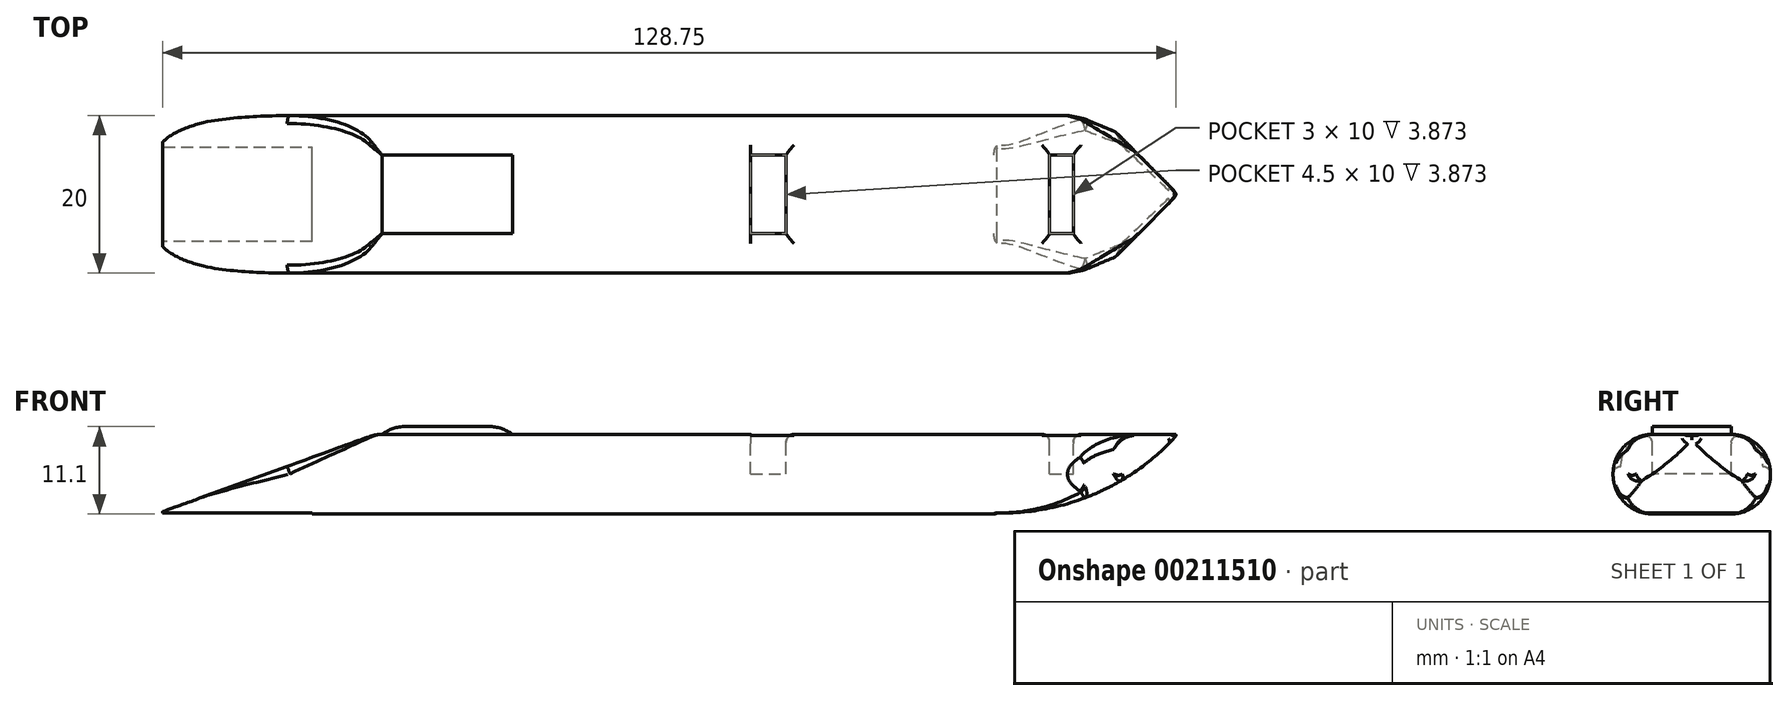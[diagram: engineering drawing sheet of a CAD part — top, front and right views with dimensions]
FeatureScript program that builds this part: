
annotation { "Feature Type Name" : "Feature", "Feature Type Description" : "" }
export const myFeature = defineFeature(function(context is Context, id is Id, definition is map)
    precondition{}
    {
        {
            var Q0;
            Q0=qCreatedBy(makeId("Top.planeOp"),FACE);
            var sketch = newSketch(context, id + "F0", { "sketchPlane" : qUnion([Q0])});
            skLineSegment(sketch, "E0.bottom", {"start": v(-64.41, 48.03) * mm, "end": v(65.59, 48.03) * mm});
            skLineSegment(sketch, "E0.top", {"start": v(-64.41, 28.03) * mm, "end": v(65.59, 28.03) * mm});
            skLineSegment(sketch, "E0.left", {"start": v(-64.41, 48.03) * mm, "end": v(-64.41, 28.03) * mm});
            skLineSegment(sketch, "E0.right", {"start": v(65.59, 48.03) * mm, "end": v(65.59, 28.03) * mm});
            skSolve(sketch);
        }
        {
            var Q0;
            Q0 = qSketchRegion(id + "F0", true);
            extrude(context, id + "F1", {"entities" : qUnion([Q0]), "depth" : 10 * mm});
        }
        {
            var Q0;
            Q0=makeQuery(id+"F1.opExtrude","CAP_EDGE",EDGE,{"disambiguationData":[OSD([sQuery(id+"F0.wireOp",EDGE,"E0.left")])],"isStart":false});
            chamfer(context, id + "F2", {"entities" : qUnion([Q0]), "chamferType" : ChamferType.OFFSET_ANGLE, "width" : 28 * mm, "oppositeDirection" : false, "angle" : 20 * degree, "tangentPropagation" : true});
        }
        {
            var Q0;
            Q0=makeQuery(id+"F1.opExtrude","SWEPT_EDGE",EDGE,{"disambiguationData":[OSD([sQuery(id+"F0.wireOp",EDGE,"E0.bottom"),sQuery(id+"F0.wireOp",EDGE,"E0.right")])]});
            var Q1;
            Q1=makeQuery(id+"F1.opExtrude","CAP_EDGE",EDGE,{"disambiguationData":[OSD([sQuery(id+"F0.wireOp",EDGE,"E0.right")])],"isStart":true});
            var Q2;
            Q2=makeQuery(id+"F1.opExtrude","SWEPT_EDGE",EDGE,{"disambiguationData":[OSD([sQuery(id+"F0.wireOp",EDGE,"E0.top"),sQuery(id+"F0.wireOp",EDGE,"E0.right")])]});
            chamfer(context, id + "F3", {"entities" : qUnion([Q0, Q1, Q2]), "chamferType" : ChamferType.OFFSET_ANGLE, "width" : 10 * mm, "oppositeDirection" : false, "angle" : 45 * degree, "tangentPropagation" : true});
        }
        {
            var Q0;
            {var subQ0=sQuery(id+"F0.wireOp",EDGE,"E0.right");Q0=makeQuery(id+"F3.opChamfer","BLEND_EDGE",EDGE,{"blendedFrom":[makeQuery(id+"F1.opExtrude","CAP_EDGE",EDGE,{"disambiguationData":[OSD([subQ0])],"isStart":true}),makeQuery(id+"F1.opExtrude","CAP_FACE",FACE,{"disambiguationData":[OSD([sQuery(id+"F0.wireOp",EDGE,"E0.bottom"),sQuery(id+"F0.wireOp",EDGE,"E0.top"),sQuery(id+"F0.wireOp",EDGE,"E0.left"),subQ0])],"isStart":true})],"blendedInto":[makeQuery(id+"F1.opExtrude","CAP_FACE",FACE,{"disambiguationData":[OSD([sQuery(id+"F0.wireOp",EDGE,"E0.bottom"),sQuery(id+"F0.wireOp",EDGE,"E0.top"),sQuery(id+"F0.wireOp",EDGE,"E0.left"),subQ0])],"isStart":true})]});}
            fillet(context, id + "F4", {"entities" : qUnion([Q0]), "radius" : 30 * mm, "tangentPropagation" : true, "allowEdgeOverflow" : false});
        }
        {
            var Q0;
            {var subQ0=sQuery(id+"F0.wireOp",EDGE,"E0.top");Q0=makeQuery(id+"F3.opChamfer","BLEND_EDGE",EDGE,{"blendedFrom":[makeQuery(id+"F1.opExtrude","SWEPT_EDGE",EDGE,{"disambiguationData":[OSD([subQ0,sQuery(id+"F0.wireOp",EDGE,"E0.right")])]}),makeQuery(id+"F1.opExtrude","SWEPT_FACE",FACE,{"disambiguationData":[OSD([subQ0])]})],"blendedInto":[makeQuery(id+"F1.opExtrude","SWEPT_FACE",FACE,{"disambiguationData":[OSD([subQ0])]})]});}
            var Q1;
            {var subQ0=sQuery(id+"F0.wireOp",EDGE,"E0.bottom");Q1=makeQuery(id+"F3.opChamfer","BLEND_EDGE",EDGE,{"blendedFrom":[makeQuery(id+"F1.opExtrude","SWEPT_EDGE",EDGE,{"disambiguationData":[OSD([subQ0,sQuery(id+"F0.wireOp",EDGE,"E0.right")])]}),makeQuery(id+"F1.opExtrude","SWEPT_FACE",FACE,{"disambiguationData":[OSD([subQ0])]})],"blendedInto":[makeQuery(id+"F1.opExtrude","SWEPT_FACE",FACE,{"disambiguationData":[OSD([subQ0])]})]});}
            chamfer(context, id + "F5", {"entities" : qUnion([Q0, Q1]), "width" : 7 * mm, "tangentPropagation" : true});
        }
        {
            var Q0;
            {var subQ0=sQuery(id+"F0.wireOp",EDGE,"E0.top");var subQ1=makeQuery(id+"F1.opExtrude","SWEPT_FACE",FACE,{"disambiguationData":[OSD([subQ0])]});Q0=makeQuery(id+"F5.opChamfer","BLEND_EDGE",EDGE,{"blendedFrom":[makeQuery(id+"F3.opChamfer","BLEND_EDGE",EDGE,{"blendedFrom":[makeQuery(id+"F1.opExtrude","SWEPT_EDGE",EDGE,{"disambiguationData":[OSD([subQ0,sQuery(id+"F0.wireOp",EDGE,"E0.right")])]}),subQ1],"blendedInto":[subQ1]}),subQ1],"blendedInto":[subQ1]});}
            var Q1;
            {var subQ0=sQuery(id+"F0.wireOp",EDGE,"E0.bottom");var subQ1=makeQuery(id+"F1.opExtrude","SWEPT_FACE",FACE,{"disambiguationData":[OSD([subQ0])]});Q1=makeQuery(id+"F5.opChamfer","BLEND_EDGE",EDGE,{"blendedFrom":[makeQuery(id+"F3.opChamfer","BLEND_EDGE",EDGE,{"blendedFrom":[makeQuery(id+"F1.opExtrude","SWEPT_EDGE",EDGE,{"disambiguationData":[OSD([subQ0,sQuery(id+"F0.wireOp",EDGE,"E0.right")])]}),subQ1],"blendedInto":[subQ1]}),subQ1],"blendedInto":[subQ1]});}
            chamfer(context, id + "F6", {"entities" : qUnion([Q0, Q1]), "width" : 5 * mm, "tangentPropagation" : true});
        }
        {
            var Q0;
            Q0=makeQuery(id+"F2.opChamfer","BLEND_EDGE",EDGE,{"blendedFrom":[makeQuery(id+"F1.opExtrude","CAP_EDGE",EDGE,{"disambiguationData":[OSD([sQuery(id+"F0.wireOp",EDGE,"E0.left")])],"isStart":false}),makeQuery(id+"F1.opExtrude","SWEPT_FACE",FACE,{"disambiguationData":[OSD([sQuery(id+"F0.wireOp",EDGE,"E0.top")])]})],"blendedInto":[makeQuery(id+"F1.opExtrude","SWEPT_FACE",FACE,{"disambiguationData":[OSD([sQuery(id+"F0.wireOp",EDGE,"E0.top")])]})]});
            var Q1;
            Q1=makeQuery(id+"F2.opChamfer","BLEND_EDGE",EDGE,{"blendedFrom":[makeQuery(id+"F1.opExtrude","CAP_EDGE",EDGE,{"disambiguationData":[OSD([sQuery(id+"F0.wireOp",EDGE,"E0.left")])],"isStart":false}),makeQuery(id+"F1.opExtrude","SWEPT_FACE",FACE,{"disambiguationData":[OSD([sQuery(id+"F0.wireOp",EDGE,"E0.bottom")])]})],"blendedInto":[makeQuery(id+"F1.opExtrude","SWEPT_FACE",FACE,{"disambiguationData":[OSD([sQuery(id+"F0.wireOp",EDGE,"E0.bottom")])]})]});
            fillet(context, id + "F7", {"entities" : qUnion([Q0, Q1]), "radius" : 1 * mm, "tangentPropagation" : true, "allowEdgeOverflow" : false});
        }
        {
            var Q0;
            {var subQ0=sQuery(id+"F0.wireOp",EDGE,"E0.left");Q0=makeQuery(id+"F2.opChamfer","BLEND_EDGE",EDGE,{"blendedFrom":[makeQuery(id+"F1.opExtrude","CAP_EDGE",EDGE,{"disambiguationData":[OSD([subQ0])],"isStart":false}),makeQuery(id+"F1.opExtrude","CAP_FACE",FACE,{"disambiguationData":[OSD([sQuery(id+"F0.wireOp",EDGE,"E0.bottom"),sQuery(id+"F0.wireOp",EDGE,"E0.top"),subQ0,sQuery(id+"F0.wireOp",EDGE,"E0.right")])],"isStart":false})],"blendedInto":[makeQuery(id+"F1.opExtrude","CAP_FACE",FACE,{"disambiguationData":[OSD([sQuery(id+"F0.wireOp",EDGE,"E0.bottom"),sQuery(id+"F0.wireOp",EDGE,"E0.top"),subQ0,sQuery(id+"F0.wireOp",EDGE,"E0.right")])],"isStart":false})]});}
            fillet(context, id + "F8", {"entities" : qUnion([Q0]), "radius" : 5 * mm, "tangentPropagation" : true, "allowEdgeOverflow" : false});
        }
        {
            var Q0;
            Q0=makeQuery(id+"F1.opExtrude","CAP_FACE",FACE,{"disambiguationData":[OSD([sQuery(id+"F0.wireOp",EDGE,"E0.bottom"),sQuery(id+"F0.wireOp",EDGE,"E0.top"),sQuery(id+"F0.wireOp",EDGE,"E0.left"),sQuery(id+"F0.wireOp",EDGE,"E0.right")])],"isStart":false});
            var sketch = newSketch(context, id + "F9", { "sketchPlane" : qUnion([Q0])});
            skLineSegment(sketch, "E1.bottom", {"start": v(52.29, 43.03) * mm, "end": v(49.29, 43.03) * mm});
            skLineSegment(sketch, "E1.top", {"start": v(52.29, 33.03) * mm, "end": v(49.29, 33.03) * mm});
            skLineSegment(sketch, "E1.left", {"start": v(52.29, 43.03) * mm, "end": v(52.29, 33.03) * mm});
            skLineSegment(sketch, "E1.right", {"start": v(49.29, 43.03) * mm, "end": v(49.29, 33.03) * mm});
            skLineSegment(sketch, "E2.bottom", {"start": v(-31.53, 43.03) * mm, "end": v(-23.03, 43.03) * mm});
            skLineSegment(sketch, "E2.top", {"start": v(-31.53, 33.03) * mm, "end": v(-23.03, 33.03) * mm});
            skLineSegment(sketch, "E2.left", {"start": v(-31.53, 43.03) * mm, "end": v(-31.53, 33.03) * mm});
            skLineSegment(sketch, "E2.right", {"start": v(-23.03, 43.03) * mm, "end": v(-23.03, 33.03) * mm});
            skLineSegment(sketch, "E3.bottom", {"start": v(11.3, 43.03) * mm, "end": v(15.8, 43.03) * mm});
            skLineSegment(sketch, "E3.top", {"start": v(11.3, 33.03) * mm, "end": v(15.8, 33.03) * mm});
            skLineSegment(sketch, "E3.left", {"start": v(11.3, 43.03) * mm, "end": v(11.3, 33.03) * mm});
            skLineSegment(sketch, "E3.right", {"start": v(15.8, 43.03) * mm, "end": v(15.8, 33.03) * mm});
            skSolve(sketch);
        }
        {
            var Q0;
            Q0=makeQuery(id+"F9.imprint","IMPRINT",FACE,{"disambiguationData":[TD([[makeQuery(id+"F9.imprint","IMPRINT",EDGE,{"derivedFrom":sQuery(id+"F9.wireOp",EDGE,"E3.bottom")}),1.0]])]});
            var Q1;
            Q1=makeQuery(id+"F9.imprint","IMPRINT",FACE,{"disambiguationData":[TD([[makeQuery(id+"F9.imprint","IMPRINT",EDGE,{"derivedFrom":sQuery(id+"F9.wireOp",EDGE,"E1.bottom")}),1.0]])]});
            extrude(context, id + "F10", {"entities" : qUnion([Q0, Q1]), "operationType" : NewBodyOperationType.REMOVE, "oppositeDirection" : true, "depth" : 5 * mm});
        }
        {
            var Q0;
            {var subQ0=sQuery(id+"F0.wireOp",EDGE,"E0.right");var subQ1=sQuery(id+"F0.wireOp",EDGE,"E0.top");Q0=makeQuery(id+"F4.opFillet","BLEND_EDGE",EDGE,{"blendedFrom":[makeQuery(id+"F3.opChamfer","BLEND_EDGE",EDGE,{"blendedFrom":[makeQuery(id+"F1.opExtrude","CAP_EDGE",EDGE,{"disambiguationData":[OSD([subQ0])],"isStart":true}),makeQuery(id+"F1.opExtrude","CAP_FACE",FACE,{"disambiguationData":[OSD([sQuery(id+"F0.wireOp",EDGE,"E0.bottom"),subQ1,sQuery(id+"F0.wireOp",EDGE,"E0.left"),subQ0])],"isStart":true})],"blendedInto":[makeQuery(id+"F1.opExtrude","CAP_FACE",FACE,{"disambiguationData":[OSD([sQuery(id+"F0.wireOp",EDGE,"E0.bottom"),subQ1,sQuery(id+"F0.wireOp",EDGE,"E0.left"),subQ0])],"isStart":true})]}),makeQuery(id+"F3.opChamfer","BLEND_FACE",FACE,{"disambiguationData":[OSD([subQ1,subQ0])]})],"blendedInto":[makeQuery(id+"F3.opChamfer","BLEND_FACE",FACE,{"disambiguationData":[OSD([subQ1,subQ0])]})]});}
            var Q1;
            {var subQ0=sQuery(id+"F0.wireOp",EDGE,"E0.right");var subQ1=sQuery(id+"F0.wireOp",EDGE,"E0.bottom");Q1=makeQuery(id+"F4.opFillet","BLEND_EDGE",EDGE,{"blendedFrom":[makeQuery(id+"F3.opChamfer","BLEND_EDGE",EDGE,{"blendedFrom":[makeQuery(id+"F1.opExtrude","CAP_EDGE",EDGE,{"disambiguationData":[OSD([subQ0])],"isStart":true}),makeQuery(id+"F1.opExtrude","CAP_FACE",FACE,{"disambiguationData":[OSD([subQ1,sQuery(id+"F0.wireOp",EDGE,"E0.top"),sQuery(id+"F0.wireOp",EDGE,"E0.left"),subQ0])],"isStart":true})],"blendedInto":[makeQuery(id+"F1.opExtrude","CAP_FACE",FACE,{"disambiguationData":[OSD([subQ1,sQuery(id+"F0.wireOp",EDGE,"E0.top"),sQuery(id+"F0.wireOp",EDGE,"E0.left"),subQ0])],"isStart":true})]}),makeQuery(id+"F3.opChamfer","BLEND_FACE",FACE,{"disambiguationData":[OSD([subQ1,subQ0])]})],"blendedInto":[makeQuery(id+"F3.opChamfer","BLEND_FACE",FACE,{"disambiguationData":[OSD([subQ1,subQ0])]})]});}
            fillet(context, id + "F11", {"entities" : qUnion([Q0, Q1]), "radius" : 1 * mm, "tangentPropagation" : true, "allowEdgeOverflow" : false});
        }
        {
            var Q0;
            {var subQ0=sQuery(id+"F0.wireOp",EDGE,"E0.bottom");var subQ1=sQuery(id+"F0.wireOp",EDGE,"E0.right");var subQ2=sQuery(id+"F0.wireOp",EDGE,"E0.left");var subQ3=sQuery(id+"F0.wireOp",EDGE,"E0.top");var subQ4=makeQuery(id+"F1.opExtrude","CAP_FACE",FACE,{"disambiguationData":[OSD([subQ0,subQ3,subQ2,subQ1])],"isStart":false});var subQ5=subQ4;Q0=makeQuery(id+"F10.boolean.opBoolean","SPLIT",FACE,{"disambiguationData":[TD([makeQuery(id+"F10.opExtrude","SWEPT_FACE",FACE,{"disambiguationData":[OSD([sQuery(id+"F9.wireOp",EDGE,"E3.left")])]})])],"derivedFrom":subQ5});}
            var sketch = newSketch(context, id + "F12", { "sketchPlane" : qUnion([Q0])});
            skLineSegment(sketch, "E4", {"start": v(-18.95, 33.03) * mm, "end": v(-18.95, 43.03) * mm});
            skSolve(sketch);
        }
        {
            var Q0;
            {var subQ0=sQuery(id+"F12.wireOp",EDGE,"E4");Q0=makeQuery(id+"F12.imprint","IMPRINT",FACE,{"disambiguationData":[TD([[makeQuery(id+"F12.imprint","IMPRINT",EDGE,{"derivedFrom":subQ0}),1.0]])]});}
            extrude(context, id + "F13", {"entities" : qUnion([Q0]), "operationType" : NewBodyOperationType.ADD, "depth" : 1 * mm});
        }
        {
            var Q0;
            Q0=makeQuery(id+"F13.opExtrude","CAP_EDGE",EDGE,{"disambiguationData":[OSD([sQuery(id+"F12.wireOp",EDGE,"E4")])],"isStart":false});
            fillet(context, id + "F14", {"entities" : qUnion([Q0]), "radius" : 5 * mm, "tangentPropagation" : true, "allowEdgeOverflow" : false});
        }
        {
            var Q0;
            {var subQ0=sQuery(id+"F0.wireOp",EDGE,"E0.right");var subQ1=sQuery(id+"F0.wireOp",EDGE,"E0.left");var subQ2=sQuery(id+"F0.wireOp",EDGE,"E0.top");var subQ3=sQuery(id+"F0.wireOp",EDGE,"E0.bottom");var subQ4=makeQuery(id+"F1.opExtrude","CAP_FACE",FACE,{"disambiguationData":[OSD([subQ3,subQ2,subQ1,subQ0])],"isStart":false});Q0=makeQuery(id+"F13.opExtrude","CAP_EDGE",EDGE,{"disambiguationData":[OSD([subQ3,subQ2,subQ1,subQ0]),TDD([makeQuery(id+"F12.imprint","IMPRINT",EDGE,{"derivedFrom":makeQuery(id+"F8.opFillet","BLEND_EDGE",EDGE,{"blendedFrom":[makeQuery(id+"F2.opChamfer","BLEND_EDGE",EDGE,{"blendedFrom":[makeQuery(id+"F1.opExtrude","CAP_EDGE",EDGE,{"disambiguationData":[OSD([subQ1])],"isStart":false}),subQ4],"blendedInto":[subQ4]}),subQ4],"blendedInto":[subQ4]})})])],"isStart":false});}
            fillet(context, id + "F15", {"entities" : qUnion([Q0]), "radius" : 5 * mm, "tangentPropagation" : true, "allowEdgeOverflow" : false});
        }
        {
            var Q0;
            Q0=makeQuery(id+"F1.opExtrude","CAP_FACE",FACE,{"disambiguationData":[OSD([sQuery(id+"F0.wireOp",EDGE,"E0.bottom"),sQuery(id+"F0.wireOp",EDGE,"E0.top"),sQuery(id+"F0.wireOp",EDGE,"E0.left"),sQuery(id+"F0.wireOp",EDGE,"E0.right")])],"isStart":true});
            var sketch = newSketch(context, id + "F16", { "sketchPlane" : qUnion([Q0])});
            skLineSegment(sketch, "E5.bottom", {"start": v(-44.4, -28.03) * mm, "end": v(42.6, -28.03) * mm});
            skLineSegment(sketch, "E5.top", {"start": v(-44.4, -48.03) * mm, "end": v(42.6, -48.03) * mm});
            skLineSegment(sketch, "E5.left", {"start": v(-44.4, -28.03) * mm, "end": v(-44.4, -48.03) * mm});
            skLineSegment(sketch, "E5.right", {"start": v(42.6, -28.03) * mm, "end": v(42.6, -48.03) * mm});
            skSolve(sketch);
        }
        {
            var Q0;
            Q0 = qSketchRegion(id + "F16", true);
            extrude(context, id + "F17", {"entities" : qUnion([Q0]), "operationType" : NewBodyOperationType.ADD, "depth" : 0.1 * mm});
        }
        {
            var Q0;
            Q0=makeQuery(id+"F17.opExtrude","CAP_EDGE",EDGE,{"disambiguationData":[OSD([sQuery(id+"F16.wireOp",EDGE,"E5.bottom")])],"isStart":false});
            var Q1;
            Q1=makeQuery(id+"F17.opExtrude","CAP_EDGE",EDGE,{"disambiguationData":[OSD([sQuery(id+"F16.wireOp",EDGE,"E5.top")])],"isStart":false});
            fillet(context, id + "F18", {"entities" : qUnion([Q0, Q1]), "radius" : 5 * mm, "tangentPropagation" : true, "allowEdgeOverflow" : false});
        }
        {
            var Q0;
            {var subQ0=sQuery(id+"F0.wireOp",EDGE,"E0.right");var subQ1=sQuery(id+"F0.wireOp",EDGE,"E0.top");Q0=makeQuery(id+"F3.opChamfer","BLEND_EDGE",EDGE,{"blendedFrom":[makeQuery(id+"F1.opExtrude","SWEPT_EDGE",EDGE,{"disambiguationData":[OSD([subQ1,subQ0])]}),makeQuery(id+"F1.opExtrude","CAP_FACE",FACE,{"disambiguationData":[OSD([sQuery(id+"F0.wireOp",EDGE,"E0.bottom"),subQ1,sQuery(id+"F0.wireOp",EDGE,"E0.left"),subQ0])],"isStart":false})],"blendedInto":[makeQuery(id+"F1.opExtrude","CAP_FACE",FACE,{"disambiguationData":[OSD([sQuery(id+"F0.wireOp",EDGE,"E0.bottom"),subQ1,sQuery(id+"F0.wireOp",EDGE,"E0.left"),subQ0])],"isStart":false})]});}
            var Q1;
            {var subQ0=sQuery(id+"F0.wireOp",EDGE,"E0.right");var subQ1=sQuery(id+"F0.wireOp",EDGE,"E0.bottom");Q1=makeQuery(id+"F3.opChamfer","BLEND_EDGE",EDGE,{"blendedFrom":[makeQuery(id+"F1.opExtrude","SWEPT_EDGE",EDGE,{"disambiguationData":[OSD([subQ1,subQ0])]}),makeQuery(id+"F1.opExtrude","CAP_FACE",FACE,{"disambiguationData":[OSD([subQ1,sQuery(id+"F0.wireOp",EDGE,"E0.top"),sQuery(id+"F0.wireOp",EDGE,"E0.left"),subQ0])],"isStart":false})],"blendedInto":[makeQuery(id+"F1.opExtrude","CAP_FACE",FACE,{"disambiguationData":[OSD([subQ1,sQuery(id+"F0.wireOp",EDGE,"E0.top"),sQuery(id+"F0.wireOp",EDGE,"E0.left"),subQ0])],"isStart":false})]});}
            var Q2;
            {var subQ0=sQuery(id+"F0.wireOp",EDGE,"E0.right");var subQ1=sQuery(id+"F0.wireOp",EDGE,"E0.top");var subQ2=makeQuery(id+"F1.opExtrude","SWEPT_FACE",FACE,{"disambiguationData":[OSD([subQ1])]});Q2=makeQuery(id+"F6.opChamfer","BLEND_EDGE",EDGE,{"blendedFrom":[makeQuery(id+"F5.opChamfer","BLEND_EDGE",EDGE,{"blendedFrom":[makeQuery(id+"F3.opChamfer","BLEND_EDGE",EDGE,{"blendedFrom":[makeQuery(id+"F1.opExtrude","SWEPT_EDGE",EDGE,{"disambiguationData":[OSD([subQ1,subQ0])]}),subQ2],"blendedInto":[subQ2]}),subQ2],"blendedInto":[subQ2]}),makeQuery(id+"F5.opChamfer","BLEND_FACE",FACE,{"disambiguationData":[OSD([subQ1,subQ0])]})],"blendedInto":[makeQuery(id+"F5.opChamfer","BLEND_FACE",FACE,{"disambiguationData":[OSD([subQ1,subQ0])]})]});}
            var Q3;
            {var subQ0=sQuery(id+"F0.wireOp",EDGE,"E0.right");var subQ1=sQuery(id+"F0.wireOp",EDGE,"E0.bottom");var subQ2=makeQuery(id+"F1.opExtrude","SWEPT_FACE",FACE,{"disambiguationData":[OSD([subQ1])]});Q3=makeQuery(id+"F6.opChamfer","BLEND_EDGE",EDGE,{"blendedFrom":[makeQuery(id+"F5.opChamfer","BLEND_EDGE",EDGE,{"blendedFrom":[makeQuery(id+"F3.opChamfer","BLEND_EDGE",EDGE,{"blendedFrom":[makeQuery(id+"F1.opExtrude","SWEPT_EDGE",EDGE,{"disambiguationData":[OSD([subQ1,subQ0])]}),subQ2],"blendedInto":[subQ2]}),subQ2],"blendedInto":[subQ2]}),makeQuery(id+"F5.opChamfer","BLEND_FACE",FACE,{"disambiguationData":[OSD([subQ1,subQ0])]})],"blendedInto":[makeQuery(id+"F5.opChamfer","BLEND_FACE",FACE,{"disambiguationData":[OSD([subQ1,subQ0])]})]});}
            fillet(context, id + "F19", {"entities" : qUnion([Q0, Q1, Q2, Q3]), "radius" : 0.1 * mm, "tangentPropagation" : true, "allowEdgeOverflow" : false});
        }
        {
            var Q0;
            Q0=makeQuery(id+"F10.boolean.opBoolean","COPY",EDGE,{"derivedFrom":makeQuery(id+"F10.opExtrude","CAP_EDGE",EDGE,{"disambiguationData":[OSD([sQuery(id+"F9.wireOp",EDGE,"E1.right")])],"isStart":true})});
            var Q1;
            {var subQ0=sQuery(id+"F0.wireOp",EDGE,"E0.bottom");Q1=makeQuery(id+"F10.boolean.opBoolean","MERGE",EDGE,{"derivedFrom":[makeQuery(id+"F8.opFillet","BLEND_EDGE",EDGE,{"blendedFrom":[makeQuery(id+"F1.opExtrude","CAP_EDGE",EDGE,{"disambiguationData":[OSD([subQ0])],"isStart":false}),makeQuery(id+"F1.opExtrude","CAP_FACE",FACE,{"disambiguationData":[OSD([subQ0,sQuery(id+"F0.wireOp",EDGE,"E0.top"),sQuery(id+"F0.wireOp",EDGE,"E0.left"),sQuery(id+"F0.wireOp",EDGE,"E0.right")])],"isStart":false})],"blendedInto":[makeQuery(id+"F1.opExtrude","CAP_FACE",FACE,{"disambiguationData":[OSD([subQ0,sQuery(id+"F0.wireOp",EDGE,"E0.top"),sQuery(id+"F0.wireOp",EDGE,"E0.left"),sQuery(id+"F0.wireOp",EDGE,"E0.right")])],"isStart":false})]}),makeQuery(id+"F10.opExtrude","CAP_EDGE",EDGE,{"disambiguationData":[OSD([sQuery(id+"F9.wireOp",EDGE,"E1.bottom")])],"isStart":true})]});}
            var Q2;
            Q2=makeQuery(id+"F10.boolean.opBoolean","COPY",EDGE,{"derivedFrom":makeQuery(id+"F10.opExtrude","CAP_EDGE",EDGE,{"disambiguationData":[OSD([sQuery(id+"F9.wireOp",EDGE,"E1.left")])],"isStart":true})});
            var Q3;
            {var subQ0=sQuery(id+"F0.wireOp",EDGE,"E0.top");Q3=makeQuery(id+"F10.boolean.opBoolean","MERGE",EDGE,{"derivedFrom":[makeQuery(id+"F8.opFillet","BLEND_EDGE",EDGE,{"blendedFrom":[makeQuery(id+"F1.opExtrude","CAP_EDGE",EDGE,{"disambiguationData":[OSD([subQ0])],"isStart":false}),makeQuery(id+"F1.opExtrude","CAP_FACE",FACE,{"disambiguationData":[OSD([sQuery(id+"F0.wireOp",EDGE,"E0.bottom"),subQ0,sQuery(id+"F0.wireOp",EDGE,"E0.left"),sQuery(id+"F0.wireOp",EDGE,"E0.right")])],"isStart":false})],"blendedInto":[makeQuery(id+"F1.opExtrude","CAP_FACE",FACE,{"disambiguationData":[OSD([sQuery(id+"F0.wireOp",EDGE,"E0.bottom"),subQ0,sQuery(id+"F0.wireOp",EDGE,"E0.left"),sQuery(id+"F0.wireOp",EDGE,"E0.right")])],"isStart":false})]}),makeQuery(id+"F10.opExtrude","CAP_EDGE",EDGE,{"disambiguationData":[OSD([sQuery(id+"F9.wireOp",EDGE,"E1.top")])],"isStart":true})]});}
            fillet(context, id + "F20", {"entities" : qUnion([Q0, Q1, Q2, Q3]), "radius" : 1 * mm, "tangentPropagation" : true, "allowEdgeOverflow" : false});
        }
        {
            var Q0;
            Q0=makeQuery(id+"F10.boolean.opBoolean","COPY",EDGE,{"derivedFrom":makeQuery(id+"F10.opExtrude","CAP_EDGE",EDGE,{"disambiguationData":[OSD([sQuery(id+"F9.wireOp",EDGE,"E3.left")])],"isStart":true})});
            var Q1;
            Q1=makeQuery(id+"F10.boolean.opBoolean","COPY",EDGE,{"derivedFrom":makeQuery(id+"F10.opExtrude","CAP_EDGE",EDGE,{"disambiguationData":[OSD([sQuery(id+"F9.wireOp",EDGE,"E3.right")])],"isStart":true})});
            var Q2;
            {var subQ0=sQuery(id+"F0.wireOp",EDGE,"E0.top");Q2=makeQuery(id+"F10.boolean.opBoolean","MERGE",EDGE,{"derivedFrom":[makeQuery(id+"F8.opFillet","BLEND_EDGE",EDGE,{"blendedFrom":[makeQuery(id+"F1.opExtrude","CAP_EDGE",EDGE,{"disambiguationData":[OSD([subQ0])],"isStart":false}),makeQuery(id+"F1.opExtrude","CAP_FACE",FACE,{"disambiguationData":[OSD([sQuery(id+"F0.wireOp",EDGE,"E0.bottom"),subQ0,sQuery(id+"F0.wireOp",EDGE,"E0.left"),sQuery(id+"F0.wireOp",EDGE,"E0.right")])],"isStart":false})],"blendedInto":[makeQuery(id+"F1.opExtrude","CAP_FACE",FACE,{"disambiguationData":[OSD([sQuery(id+"F0.wireOp",EDGE,"E0.bottom"),subQ0,sQuery(id+"F0.wireOp",EDGE,"E0.left"),sQuery(id+"F0.wireOp",EDGE,"E0.right")])],"isStart":false})]}),makeQuery(id+"F10.opExtrude","CAP_EDGE",EDGE,{"disambiguationData":[OSD([sQuery(id+"F9.wireOp",EDGE,"E3.top")])],"isStart":true})]});}
            var Q3;
            {var subQ0=sQuery(id+"F0.wireOp",EDGE,"E0.bottom");Q3=makeQuery(id+"F10.boolean.opBoolean","MERGE",EDGE,{"derivedFrom":[makeQuery(id+"F8.opFillet","BLEND_EDGE",EDGE,{"blendedFrom":[makeQuery(id+"F1.opExtrude","CAP_EDGE",EDGE,{"disambiguationData":[OSD([subQ0])],"isStart":false}),makeQuery(id+"F1.opExtrude","CAP_FACE",FACE,{"disambiguationData":[OSD([subQ0,sQuery(id+"F0.wireOp",EDGE,"E0.top"),sQuery(id+"F0.wireOp",EDGE,"E0.left"),sQuery(id+"F0.wireOp",EDGE,"E0.right")])],"isStart":false})],"blendedInto":[makeQuery(id+"F1.opExtrude","CAP_FACE",FACE,{"disambiguationData":[OSD([subQ0,sQuery(id+"F0.wireOp",EDGE,"E0.top"),sQuery(id+"F0.wireOp",EDGE,"E0.left"),sQuery(id+"F0.wireOp",EDGE,"E0.right")])],"isStart":false})]}),makeQuery(id+"F10.opExtrude","CAP_EDGE",EDGE,{"disambiguationData":[OSD([sQuery(id+"F9.wireOp",EDGE,"E3.bottom")])],"isStart":true})]});}
            fillet(context, id + "F21", {"entities" : qUnion([Q0, Q1, Q2, Q3]), "radius" : 1 * mm, "tangentPropagation" : true, "allowEdgeOverflow" : false});
        }
        {
            var Q0;
            {var subQ0=sQuery(id+"F0.wireOp",EDGE,"E0.right");var subQ1=sQuery(id+"F0.wireOp",EDGE,"E0.top");Q0=makeQuery(id+"F5.opChamfer","BLEND_EDGE",EDGE,{"blendedFrom":[makeQuery(id+"F3.opChamfer","BLEND_EDGE",EDGE,{"blendedFrom":[makeQuery(id+"F1.opExtrude","SWEPT_EDGE",EDGE,{"disambiguationData":[OSD([subQ1,subQ0])]}),makeQuery(id+"F1.opExtrude","SWEPT_FACE",FACE,{"disambiguationData":[OSD([subQ1])]})],"blendedInto":[makeQuery(id+"F1.opExtrude","SWEPT_FACE",FACE,{"disambiguationData":[OSD([subQ1])]})]}),makeQuery(id+"F3.opChamfer","BLEND_FACE",FACE,{"disambiguationData":[OSD([subQ1,subQ0])]})],"blendedInto":[makeQuery(id+"F3.opChamfer","BLEND_FACE",FACE,{"disambiguationData":[OSD([subQ1,subQ0])]})]});}
            var Q1;
            {var subQ0=sQuery(id+"F0.wireOp",EDGE,"E0.right");var subQ1=sQuery(id+"F0.wireOp",EDGE,"E0.top");Q1=makeQuery(id+"F5.opChamfer","BLEND_EDGE",EDGE,{"blendedFrom":[makeQuery(id+"F3.opChamfer","BLEND_EDGE",EDGE,{"blendedFrom":[makeQuery(id+"F1.opExtrude","SWEPT_EDGE",EDGE,{"disambiguationData":[OSD([subQ1,subQ0])]}),makeQuery(id+"F1.opExtrude","SWEPT_FACE",FACE,{"disambiguationData":[OSD([subQ1])]})],"blendedInto":[makeQuery(id+"F1.opExtrude","SWEPT_FACE",FACE,{"disambiguationData":[OSD([subQ1])]})]}),makeQuery(id+"F4.opFillet","BLEND_FACE",FACE,{"disambiguationData":[OSD([sQuery(id+"F0.wireOp",EDGE,"E0.bottom"),subQ1,sQuery(id+"F0.wireOp",EDGE,"E0.left"),subQ0])]})],"blendedInto":[makeQuery(id+"F4.opFillet","BLEND_FACE",FACE,{"disambiguationData":[OSD([sQuery(id+"F0.wireOp",EDGE,"E0.bottom"),subQ1,sQuery(id+"F0.wireOp",EDGE,"E0.left"),subQ0])]})]});}
            var Q2;
            Q2=makeQuery(id+"F18.opFillet","BLEND_EDGE",EDGE,{"blendedFrom":[makeQuery(id+"F17.opExtrude","CAP_EDGE",EDGE,{"disambiguationData":[OSD([sQuery(id+"F16.wireOp",EDGE,"E5.bottom")])],"isStart":false}),makeQuery(id+"F4.opFillet","BLEND_FACE",FACE,{"disambiguationData":[OSD([sQuery(id+"F0.wireOp",EDGE,"E0.bottom"),sQuery(id+"F0.wireOp",EDGE,"E0.top"),sQuery(id+"F0.wireOp",EDGE,"E0.left"),sQuery(id+"F0.wireOp",EDGE,"E0.right")])]})],"blendedInto":[makeQuery(id+"F4.opFillet","BLEND_FACE",FACE,{"disambiguationData":[OSD([sQuery(id+"F0.wireOp",EDGE,"E0.bottom"),sQuery(id+"F0.wireOp",EDGE,"E0.top"),sQuery(id+"F0.wireOp",EDGE,"E0.left"),sQuery(id+"F0.wireOp",EDGE,"E0.right")])]})]});
            var Q3;
            {var subQ0=sQuery(id+"F0.wireOp",EDGE,"E0.right");var subQ1=sQuery(id+"F0.wireOp",EDGE,"E0.top");var subQ2=makeQuery(id+"F1.opExtrude","SWEPT_FACE",FACE,{"disambiguationData":[OSD([subQ1])]});Q3=makeQuery(id+"F6.opChamfer","BLEND_EDGE",EDGE,{"blendedFrom":[makeQuery(id+"F5.opChamfer","BLEND_EDGE",EDGE,{"blendedFrom":[makeQuery(id+"F3.opChamfer","BLEND_EDGE",EDGE,{"blendedFrom":[makeQuery(id+"F1.opExtrude","SWEPT_EDGE",EDGE,{"disambiguationData":[OSD([subQ1,subQ0])]}),subQ2],"blendedInto":[subQ2]}),subQ2],"blendedInto":[subQ2]}),makeQuery(id+"F4.opFillet","BLEND_FACE",FACE,{"disambiguationData":[OSD([sQuery(id+"F0.wireOp",EDGE,"E0.bottom"),subQ1,sQuery(id+"F0.wireOp",EDGE,"E0.left"),subQ0])]})],"blendedInto":[makeQuery(id+"F4.opFillet","BLEND_FACE",FACE,{"disambiguationData":[OSD([sQuery(id+"F0.wireOp",EDGE,"E0.bottom"),subQ1,sQuery(id+"F0.wireOp",EDGE,"E0.left"),subQ0])]})]});}
            var Q4;
            {var subQ0=sQuery(id+"F0.wireOp",EDGE,"E0.right");var subQ1=sQuery(id+"F0.wireOp",EDGE,"E0.bottom");Q4=makeQuery(id+"F5.opChamfer","BLEND_EDGE",EDGE,{"blendedFrom":[makeQuery(id+"F3.opChamfer","BLEND_EDGE",EDGE,{"blendedFrom":[makeQuery(id+"F1.opExtrude","SWEPT_EDGE",EDGE,{"disambiguationData":[OSD([subQ1,subQ0])]}),makeQuery(id+"F1.opExtrude","SWEPT_FACE",FACE,{"disambiguationData":[OSD([subQ1])]})],"blendedInto":[makeQuery(id+"F1.opExtrude","SWEPT_FACE",FACE,{"disambiguationData":[OSD([subQ1])]})]}),makeQuery(id+"F3.opChamfer","BLEND_FACE",FACE,{"disambiguationData":[OSD([subQ1,subQ0])]})],"blendedInto":[makeQuery(id+"F3.opChamfer","BLEND_FACE",FACE,{"disambiguationData":[OSD([subQ1,subQ0])]})]});}
            var Q5;
            {var subQ0=sQuery(id+"F0.wireOp",EDGE,"E0.right");var subQ1=sQuery(id+"F0.wireOp",EDGE,"E0.bottom");Q5=makeQuery(id+"F5.opChamfer","BLEND_EDGE",EDGE,{"blendedFrom":[makeQuery(id+"F3.opChamfer","BLEND_EDGE",EDGE,{"blendedFrom":[makeQuery(id+"F1.opExtrude","SWEPT_EDGE",EDGE,{"disambiguationData":[OSD([subQ1,subQ0])]}),makeQuery(id+"F1.opExtrude","SWEPT_FACE",FACE,{"disambiguationData":[OSD([subQ1])]})],"blendedInto":[makeQuery(id+"F1.opExtrude","SWEPT_FACE",FACE,{"disambiguationData":[OSD([subQ1])]})]}),makeQuery(id+"F4.opFillet","BLEND_FACE",FACE,{"disambiguationData":[OSD([subQ1,sQuery(id+"F0.wireOp",EDGE,"E0.top"),sQuery(id+"F0.wireOp",EDGE,"E0.left"),subQ0])]})],"blendedInto":[makeQuery(id+"F4.opFillet","BLEND_FACE",FACE,{"disambiguationData":[OSD([subQ1,sQuery(id+"F0.wireOp",EDGE,"E0.top"),sQuery(id+"F0.wireOp",EDGE,"E0.left"),subQ0])]})]});}
            var Q6;
            {var subQ0=sQuery(id+"F0.wireOp",EDGE,"E0.right");var subQ1=sQuery(id+"F0.wireOp",EDGE,"E0.bottom");var subQ2=makeQuery(id+"F1.opExtrude","SWEPT_FACE",FACE,{"disambiguationData":[OSD([subQ1])]});Q6=makeQuery(id+"F6.opChamfer","BLEND_EDGE",EDGE,{"blendedFrom":[makeQuery(id+"F5.opChamfer","BLEND_EDGE",EDGE,{"blendedFrom":[makeQuery(id+"F3.opChamfer","BLEND_EDGE",EDGE,{"blendedFrom":[makeQuery(id+"F1.opExtrude","SWEPT_EDGE",EDGE,{"disambiguationData":[OSD([subQ1,subQ0])]}),subQ2],"blendedInto":[subQ2]}),subQ2],"blendedInto":[subQ2]}),makeQuery(id+"F4.opFillet","BLEND_FACE",FACE,{"disambiguationData":[OSD([subQ1,sQuery(id+"F0.wireOp",EDGE,"E0.top"),sQuery(id+"F0.wireOp",EDGE,"E0.left"),subQ0])]})],"blendedInto":[makeQuery(id+"F4.opFillet","BLEND_FACE",FACE,{"disambiguationData":[OSD([subQ1,sQuery(id+"F0.wireOp",EDGE,"E0.top"),sQuery(id+"F0.wireOp",EDGE,"E0.left"),subQ0])]})]});}
            var Q7;
            Q7=makeQuery(id+"F18.opFillet","BLEND_EDGE",EDGE,{"blendedFrom":[makeQuery(id+"F17.opExtrude","CAP_EDGE",EDGE,{"disambiguationData":[OSD([sQuery(id+"F16.wireOp",EDGE,"E5.top")])],"isStart":false}),makeQuery(id+"F4.opFillet","BLEND_FACE",FACE,{"disambiguationData":[OSD([sQuery(id+"F0.wireOp",EDGE,"E0.bottom"),sQuery(id+"F0.wireOp",EDGE,"E0.top"),sQuery(id+"F0.wireOp",EDGE,"E0.left"),sQuery(id+"F0.wireOp",EDGE,"E0.right")])]})],"blendedInto":[makeQuery(id+"F4.opFillet","BLEND_FACE",FACE,{"disambiguationData":[OSD([sQuery(id+"F0.wireOp",EDGE,"E0.bottom"),sQuery(id+"F0.wireOp",EDGE,"E0.top"),sQuery(id+"F0.wireOp",EDGE,"E0.left"),sQuery(id+"F0.wireOp",EDGE,"E0.right")])]})]});
            fillet(context, id + "F22", {"entities" : qUnion([Q0, Q1, Q2, Q3, Q4, Q5, Q6, Q7]), "radius" : 1.5 * mm, "tangentPropagation" : true, "allowEdgeOverflow" : false});
        }
        {
            var Q0;
            Q0=makeQuery(id+"F17.opExtrude","CAP_EDGE",EDGE,{"disambiguationData":[OSD([sQuery(id+"F16.wireOp",EDGE,"E5.right")])],"isStart":false});
            fillet(context, id + "F23", {"entities" : qUnion([Q0]), "radius" : 1 * mm, "tangentPropagation" : true, "allowEdgeOverflow" : false});
        }
        {
            var Q0;
            {var subQ0=sQuery(id+"F0.wireOp",EDGE,"E0.left");Q0=makeQuery(id+"F2.opChamfer","BLEND_EDGE",EDGE,{"blendedFrom":[makeQuery(id+"F1.opExtrude","CAP_EDGE",EDGE,{"disambiguationData":[OSD([subQ0])],"isStart":false}),makeQuery(id+"F1.opExtrude","CAP_FACE",FACE,{"disambiguationData":[OSD([sQuery(id+"F0.wireOp",EDGE,"E0.bottom"),sQuery(id+"F0.wireOp",EDGE,"E0.top"),subQ0,sQuery(id+"F0.wireOp",EDGE,"E0.right")])],"isStart":true})],"blendedInto":[makeQuery(id+"F1.opExtrude","CAP_FACE",FACE,{"disambiguationData":[OSD([sQuery(id+"F0.wireOp",EDGE,"E0.bottom"),sQuery(id+"F0.wireOp",EDGE,"E0.top"),subQ0,sQuery(id+"F0.wireOp",EDGE,"E0.right")])],"isStart":true})]});}
            fillet(context, id + "F24", {"entities" : qUnion([Q0]), "radius" : 0.1 * mm, "tangentPropagation" : true, "allowEdgeOverflow" : false});
        }
    });
